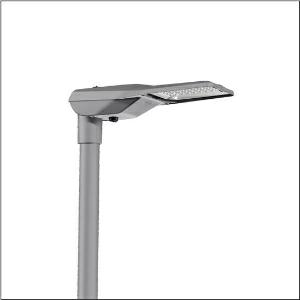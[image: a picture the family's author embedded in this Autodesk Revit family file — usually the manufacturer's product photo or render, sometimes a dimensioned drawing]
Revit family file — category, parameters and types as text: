
# Revit family: streetlight_sl_21_iq_mini___st1_0a_5xe2d41y08gb_5b29
name_source: partatom
category: Lighting Fixtures
units: mm (PartAtom-declared; Revit-internal decimal feet)

## family parameters
Cut with Voids When Loaded = No
Host = Face
Light Source = No
Part Type = Normal
Room Calculation Point = No
Round Connector Dimension = Use Diameter
Shared = No

## types (1)
- --- (1 x LED, 6190 lm, 39.8 W, 4000K)
    Apparent Load = 40 VA
    CIE Flux Codes = 37 72 97 100 100
    Color Rendering = 70
    Color Temperature = 4000K
    Default Elevation = 1800 mm
    Description = Streetlight SL 21 iQ mini, mast luminaire, primary light control with lens, of PMMA, primary optical cover: cover, of toughened safety glass, transparent, light distribution: ST1.0a, light emission: direct distribution, primary light characteristic: asymmetric, installation type: post-top, side-entry, LED, High Power LED, rated luminous flux: 6.190lm, luminous efficacy: 156lm/W, light colour: 740, colour temperature: 4000K, control: presetting dimming logarithmic, Street-Remote, Auto-Match, Temp-Guard, Lumen-Switch, Night-Set, Smart-Wire, Light-Fading, Desk-Remote (wireless, voltage-free reading and setting of iQ features in the workshop via application-optimized NFC function/RFID function), optimised constant luminous flux control (CLO 2.0), mains connection: 220..240V, AC, 50/60Hz, start of lifetime: 40W, end of service life: 41W, reduction: 18W, luminaire housing, of diecast aluminium, powder-coated, Siteco® metallic grey (DB 702S), corrosivity category C5 mid according to DIN EN ISO 12944, please order mast flange separately, inclination adjustable: 0°, 5°, 10°, 15°, sealing non-destructively replaceable, multi-level sealing system, length: 628mm, width: 235mm, height: 110mm, mast flange for spigot size: 42mm (side-entry): 5XC10008XM4, 60/48mm (side-entry/post-top): 5XC10108XM2, 76/60mm (side-entry/post-top): 5XC10108XM1, Smart Interface below and above, protection rating (complete): IP66, insulation class (complete): insulation class II (safety insulation), certification: CE, ENEC, ENEC+, VDE, impact resistance: IK09, permissible operating ambient temperature for outdoor applications: -40..+50°C, standard-compliant lighting for roads and squares, packaging unit: 1 piece

Light Distribution: ST1.0a
    Height = 110 mm
    Lamp = 1 x LED
    Lamp Light Flux = 6190 lm
    Lamp Power = 39.8 W
    Lamp count = 1
    Length = 625 mm
    Luminous efficacy = 156 lm/W
    Manufacturer = Siteco
    ModVariant = No
    Model = 5XE2D41Y08GB
    Number of Poles = 1
    OnlyDefault = Yes
    Power Factor = 1
    Product Name = Streetlight SL 21 iQ mini | ST1.0a
    Product group = mast luminaire | pylon top
    ProductGroupID = 6100
    Protection Class = Protection class II
    Protection Degree = IP 66
    RLX_Detail_Level = 1
    RLX_Emergency_Light_Flux = 0 lm
    RLX_Emergency_Type = 0
    RLX_Emergency_Type_DB = No
    RlxData = <blob elided: 92633 chars, md5=0bb2c896>
    Socket = socket
    Standby Power = 0 W
    System Light Flux = 6190 lm
    System Power = 40 W
    Type Comments = factory setting: luminous flux: 100 % | dim-lin: 254 | 800 mA
    Type Image = l_1003514.jpg
    URL = http://relux.com
    VarID = @adj_062955
    Voltage = 0 V
    Weight = 0.00 kg
    Width = 234 mm

## geometry (parser evidence)
native form markers: Blend x4, Sweep x10
no freeform markers — native parametric forms only
